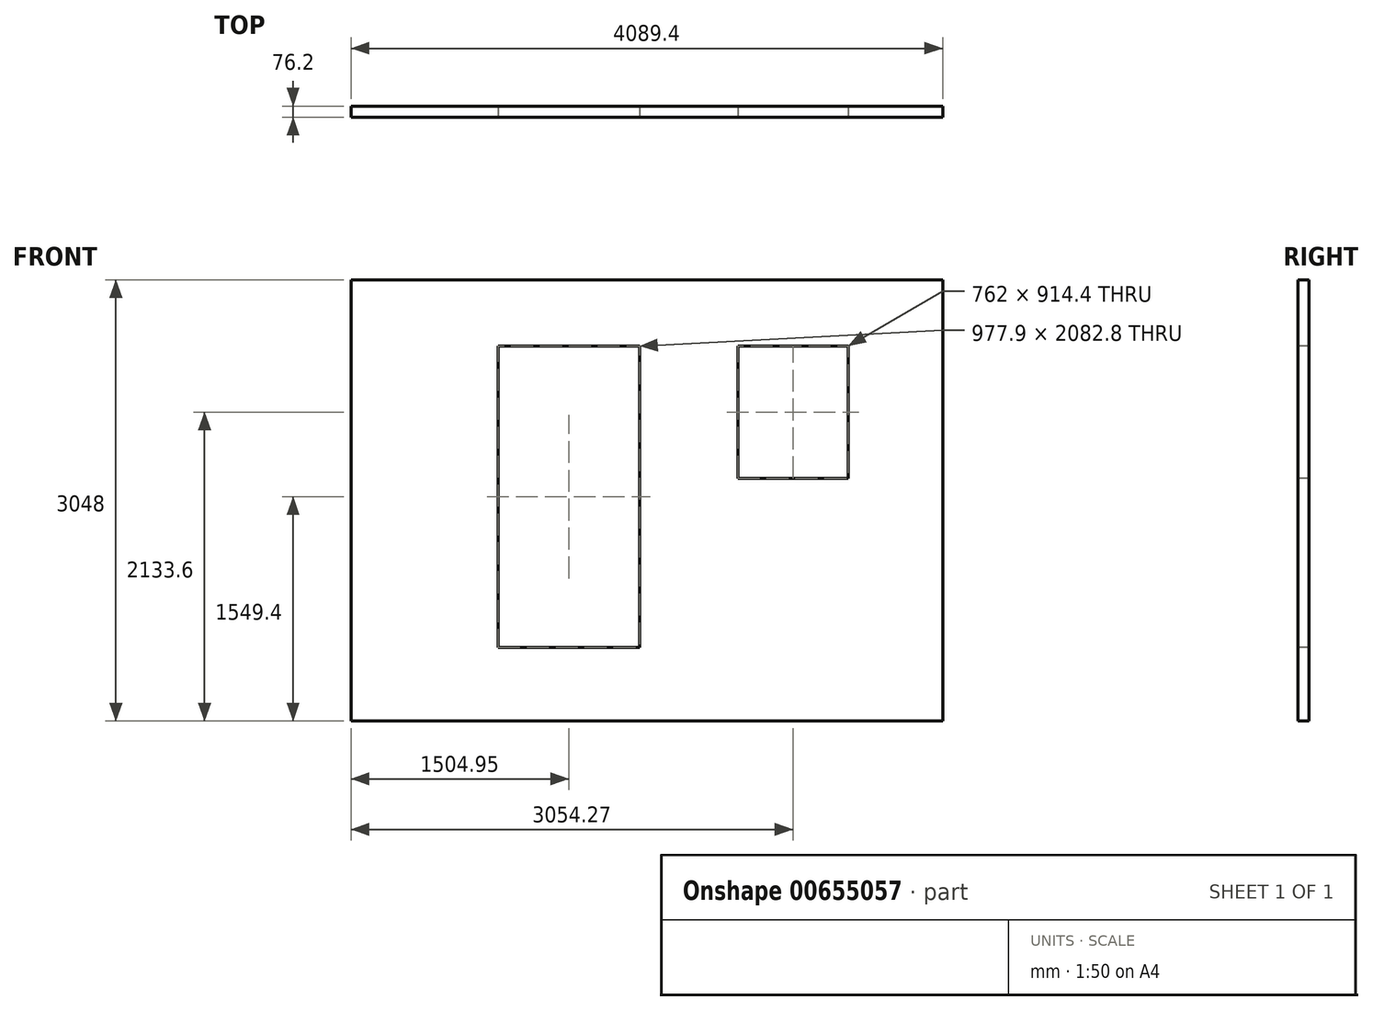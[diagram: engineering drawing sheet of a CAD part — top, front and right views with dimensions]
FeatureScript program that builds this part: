
annotation { "Feature Type Name" : "Feature", "Feature Type Description" : "" }
export const myFeature = defineFeature(function(context is Context, id is Id, definition is map)
    precondition{}
    {
        {
            var Q0;
            Q0=qCreatedBy(makeId("Top.planeOp"),FACE);
            var sketch = newSketch(context, id + "F0", { "sketchPlane" : qUnion([Q0])});
            skLineSegment(sketch, "E0.bottom", {"start": v(0, 0) * mm, "end": v(-4089.4, 0) * mm});
            skLineSegment(sketch, "E0.top", {"start": v(0, -76.2) * mm, "end": v(-4089.4, -76.2) * mm});
            skLineSegment(sketch, "E0.left", {"start": v(0, 0) * mm, "end": v(0, -76.2) * mm});
            skLineSegment(sketch, "E0.right", {"start": v(-4089.4, 0) * mm, "end": v(-4089.4, -76.2) * mm});
            skSolve(sketch);
        }
        {
            var Q0;
            Q0=makeQuery(id+"F0.imprint","IMPRINT",FACE,{"disambiguationData":[TD([[makeQuery(id+"F0.imprint","IMPRINT",EDGE,{"derivedFrom":sQuery(id+"F0.wireOp",EDGE,"E0.bottom")}),1.0]])]});
            extrude(context, id + "F1", {"entities" : qUnion([Q0]), "depth" : 3048 * mm, "offsetDistance" : 25.4 * mm});
        }
        {
            var Q0;
            Q0=makeQuery(id+"F1.opExtrude","SWEPT_FACE",FACE,{"disambiguationData":[OSD([sQuery(id+"F0.wireOp",EDGE,"E0.top")])]});
            var sketch = newSketch(context, id + "F2", { "sketchPlane" : qUnion([Q0])});
            skLineSegment(sketch, "E1", {"start": v(-3073.4, 508) * mm, "end": v(-2095.5, 508) * mm});
            skLineSegment(sketch, "E2", {"start": v(-2095.5, 508) * mm, "end": v(-2095.5, 2590.8) * mm});
            skLineSegment(sketch, "E3", {"start": v(-2095.5, 2590.8) * mm, "end": v(-3073.4, 2590.8) * mm});
            skLineSegment(sketch, "E4", {"start": v(-3073.4, 2590.8) * mm, "end": v(-3073.4, 508) * mm});
            skSolve(sketch);
        }
        {
            var Q0;
            Q0=makeQuery(id+"F2.imprint","IMPRINT",FACE,{"disambiguationData":[TD([[makeQuery(id+"F2.imprint","IMPRINT",EDGE,{"derivedFrom":sQuery(id+"F2.wireOp",EDGE,"E1")}),1.0]])]});
            extrude(context, id + "F3", {"entities" : qUnion([Q0]), "operationType" : NewBodyOperationType.REMOVE, "endBound" : BoundingType.UP_TO_NEXT, "oppositeDirection" : true, "depth" : 25.4 * mm, "offsetDistance" : 25.4 * mm});
        }
        {
            var Q0;
            Q0=makeQuery(id+"F1.opExtrude","SWEPT_FACE",FACE,{"disambiguationData":[OSD([sQuery(id+"F0.wireOp",EDGE,"E0.top")])]});
            var sketch = newSketch(context, id + "F4", { "sketchPlane" : qUnion([Q0])});
            skLineSegment(sketch, "E5.bottom", {"start": v(-1416.13, 2590.8) * mm, "end": v(-654.13, 2590.8) * mm});
            skLineSegment(sketch, "E5.top", {"start": v(-1416.13, 1676.4) * mm, "end": v(-654.13, 1676.4) * mm});
            skLineSegment(sketch, "E5.left", {"start": v(-1416.13, 2590.8) * mm, "end": v(-1416.13, 1676.4) * mm});
            skLineSegment(sketch, "E5.right", {"start": v(-654.13, 2590.8) * mm, "end": v(-654.13, 1676.4) * mm});
            skSolve(sketch);
        }
        {
            var Q0;
            Q0=makeQuery(id+"F4.imprint","IMPRINT",FACE,{"disambiguationData":[TD([[makeQuery(id+"F4.imprint","IMPRINT",EDGE,{"derivedFrom":sQuery(id+"F4.wireOp",EDGE,"E5.bottom")}),-1.0]])]});
            extrude(context, id + "F5", {"entities" : qUnion([Q0]), "operationType" : NewBodyOperationType.REMOVE, "endBound" : BoundingType.UP_TO_NEXT, "oppositeDirection" : true, "depth" : 25.4 * mm, "offsetDistance" : 25.4 * mm});
        }
    });
